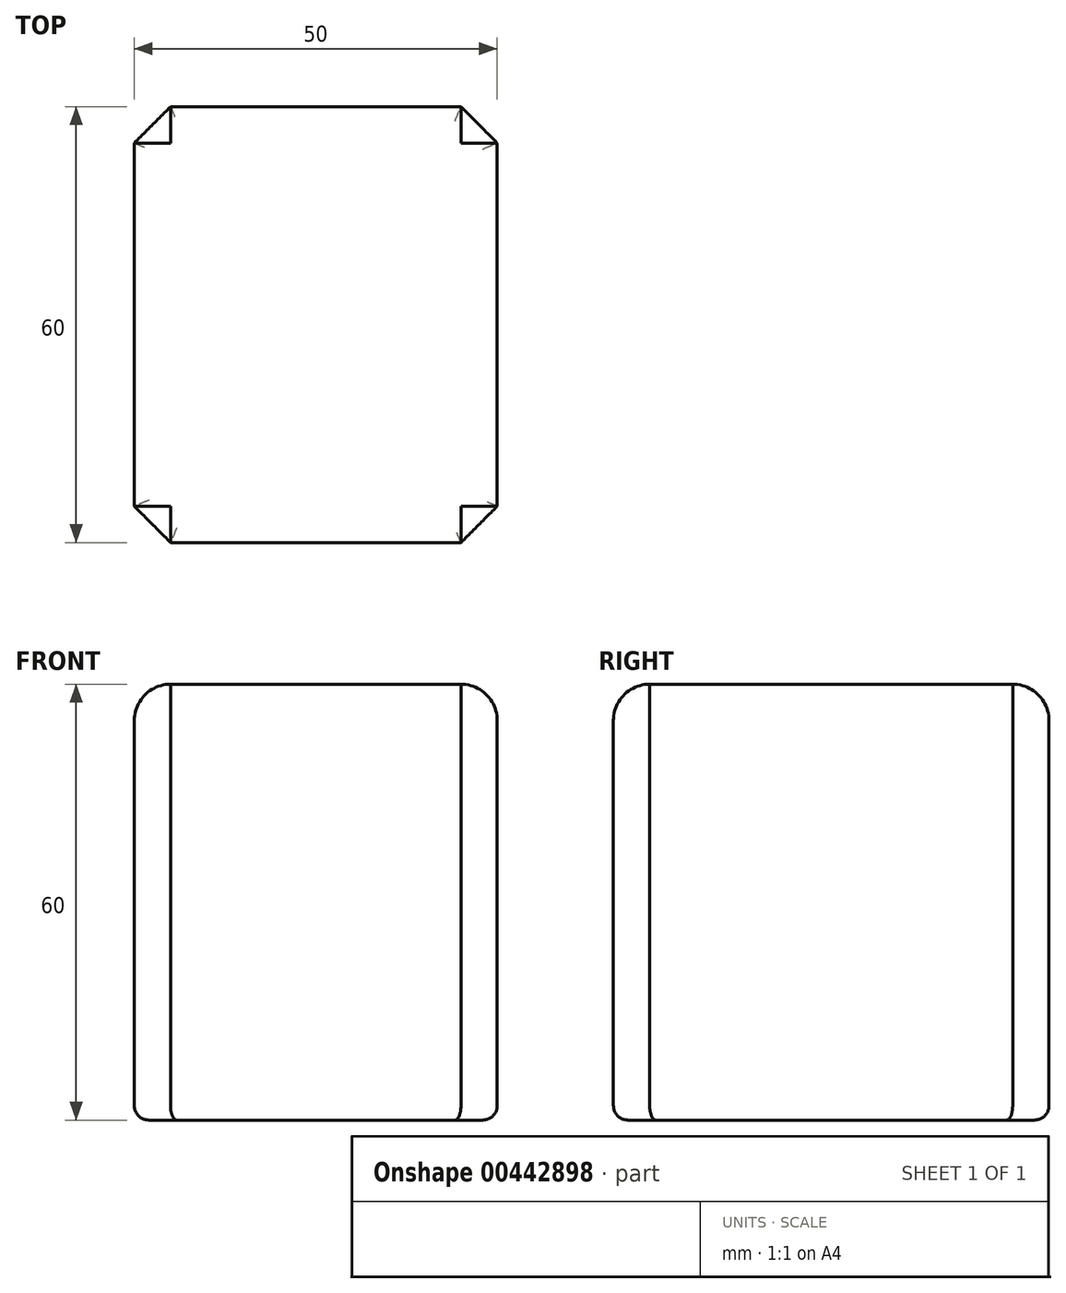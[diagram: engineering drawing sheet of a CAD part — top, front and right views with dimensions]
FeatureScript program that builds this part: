
annotation { "Feature Type Name" : "Feature", "Feature Type Description" : "" }
export const myFeature = defineFeature(function(context is Context, id is Id, definition is map)
    precondition{}
    {
        {
            var Q0;
            Q0=qCreatedBy(makeId("Top.planeOp"),FACE);
            var sketch = newSketch(context, id + "F0", { "sketchPlane" : qUnion([Q0])});
            skLineSegment(sketch, "E0.bottom", {"start": v(0, 0) * mm, "end": v(50, 0) * mm});
            skLineSegment(sketch, "E0.top", {"start": v(0, -60) * mm, "end": v(50, -60) * mm});
            skLineSegment(sketch, "E0.left", {"start": v(0, 0) * mm, "end": v(0, -60) * mm});
            skLineSegment(sketch, "E0.right", {"start": v(50, 0) * mm, "end": v(50, -60) * mm});
            skSolve(sketch);
        }
        {
            var Q0;
            Q0=makeQuery(id+"F0.imprint","IMPRINT",FACE,{"disambiguationData":[TD([[makeQuery(id+"F0.imprint","IMPRINT",EDGE,{"derivedFrom":sQuery(id+"F0.wireOp",EDGE,"E0.bottom")}),-1.0]])]});
            extrude(context, id + "F1", {"entities" : qUnion([Q0]), "depth" : 60 * mm});
        }
        {
            var Q0;
            Q0=makeQuery(id+"F1.opExtrude","CAP_FACE",FACE,{"disambiguationData":[OSD([sQuery(id+"F0.wireOp",EDGE,"E0.bottom"),sQuery(id+"F0.wireOp",EDGE,"E0.top"),sQuery(id+"F0.wireOp",EDGE,"E0.left"),sQuery(id+"F0.wireOp",EDGE,"E0.right")])],"isStart":false});
            fillet(context, id + "F2", {"entities" : qUnion([Q0]), "radius" : 5 * mm, "tangentPropagation" : true, "allowEdgeOverflow" : false});
        }
        {
            var Q0;
            Q0=makeQuery(id+"F1.opExtrude","SWEPT_EDGE",EDGE,{"disambiguationData":[OSD([sQuery(id+"F0.wireOp",EDGE,"E0.top"),sQuery(id+"F0.wireOp",EDGE,"E0.left")])]});
            var Q1;
            Q1=makeQuery(id+"F1.opExtrude","SWEPT_EDGE",EDGE,{"disambiguationData":[OSD([sQuery(id+"F0.wireOp",EDGE,"E0.top"),sQuery(id+"F0.wireOp",EDGE,"E0.right")])]});
            var Q2;
            Q2=makeQuery(id+"F1.opExtrude","SWEPT_EDGE",EDGE,{"disambiguationData":[OSD([sQuery(id+"F0.wireOp",EDGE,"E0.bottom"),sQuery(id+"F0.wireOp",EDGE,"E0.right")])]});
            var Q3;
            Q3=makeQuery(id+"F1.opExtrude","SWEPT_EDGE",EDGE,{"disambiguationData":[OSD([sQuery(id+"F0.wireOp",EDGE,"E0.bottom"),sQuery(id+"F0.wireOp",EDGE,"E0.left")])]});
            chamfer(context, id + "F3", {"entities" : qUnion([Q0, Q1, Q2, Q3]), "width" : 5 * mm, "tangentPropagation" : true});
        }
        {
            var Q0;
            Q0=makeQuery(id+"F1.opExtrude","CAP_FACE",FACE,{"disambiguationData":[OSD([sQuery(id+"F0.wireOp",EDGE,"E0.bottom"),sQuery(id+"F0.wireOp",EDGE,"E0.top"),sQuery(id+"F0.wireOp",EDGE,"E0.left"),sQuery(id+"F0.wireOp",EDGE,"E0.right")])],"isStart":true});
            fillet(context, id + "F4", {"entities" : qUnion([Q0]), "radius" : 2 * mm, "tangentPropagation" : true, "allowEdgeOverflow" : false});
        }
    });
